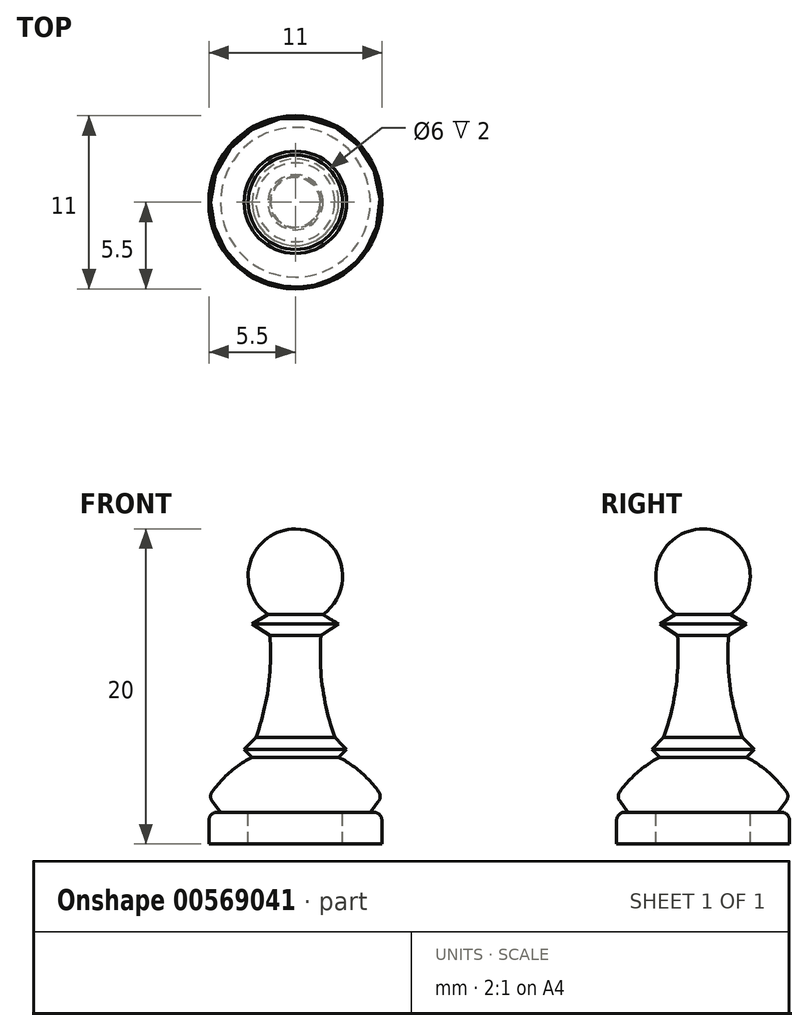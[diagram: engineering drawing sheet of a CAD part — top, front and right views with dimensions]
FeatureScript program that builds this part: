
annotation { "Feature Type Name" : "Feature", "Feature Type Description" : "" }
export const myFeature = defineFeature(function(context is Context, id is Id, definition is map)
    precondition{}
    {
        {
            var Q0;
            Q0=qCreatedBy(makeId("Front.planeOp"),FACE);
            var sketch = newSketch(context, id + "F0", { "sketchPlane" : qUnion([Q0])});
            skLineSegment(sketch, "E0", {"start": v(0, 0) * mm, "end": v(0, 20) * mm, "construction": true});
            skLineSegment(sketch, "E1", {"start": v(0, 20) * mm, "end": v(-2.87, 20) * mm, "construction": true});
            skArc(sketch, "E2", {"start": v(1.75, 14.56) * mm, "mid": v(2.86, 17.92) * mm, "end": v(0, 20) * mm});
            skLineSegment(sketch, "E3", {"start": v(1.75, 14.56) * mm, "end": v(2.75, 13.96) * mm});
            skLineSegment(sketch, "E4", {"start": v(2.75, 13.96) * mm, "end": v(1.63, 13.25) * mm});
            skArc(sketch, "E5", {"start": v(1.63, 13.25) * mm, "mid": v(1.72, 9.95) * mm, "end": v(2.5, 6.75) * mm});
            skLineSegment(sketch, "E6", {"start": v(2.5, 6.75) * mm, "end": v(3.25, 6) * mm});
            skLineSegment(sketch, "E7", {"start": v(3.25, 6) * mm, "end": v(2.75, 5.5) * mm});
            skArc(sketch, "E8", {"start": v(5.5, 3) * mm, "mid": v(4.29, 4.43) * mm, "end": v(2.75, 5.5) * mm});
            skLineSegment(sketch, "E9", {"start": v(5.5, 3) * mm, "end": v(4.76, 2) * mm});
            skLineSegment(sketch, "E10", {"start": v(4.76, 2) * mm, "end": v(5.48, 2) * mm});
            skLineSegment(sketch, "E11", {"start": v(5.48, 2) * mm, "end": v(5.5, 0) * mm});
            skLineSegment(sketch, "E12", {"start": v(5.5, 0) * mm, "end": v(3, 0) * mm});
            skLineSegment(sketch, "E13", {"start": v(0, 20) * mm, "end": v(0, 2) * mm});
            skLineSegment(sketch, "E14", {"start": v(0, 28.83) * mm, "end": v(0, -16.82) * mm, "construction": true});
            skLineSegment(sketch, "E15", {"start": v(3, 0) * mm, "end": v(3, 2) * mm});
            skLineSegment(sketch, "E16", {"start": v(3, 2) * mm, "end": v(0, 2) * mm});
            skSolve(sketch);
        }
        {
            var Q0;
            Q0=qSketchRegion(id+"F0",true);
            var Q1;
            Q1=sQuery(id+"F0.wireOp",EDGE,"E14");
            revolve(context, id + "F1", {"entities" : qUnion([Q0]), "axis" : qUnion([Q1]), "revolveType" : RevolveType.FULL});
        }
        {
            var Q0;
            Q0=makeQuery(id+"F1.opRevolve","SWEPT_EDGE",EDGE,{"disambiguationData":[OSD([sQuery(id+"F0.wireOp",EDGE,"E8"),sQuery(id+"F0.wireOp",EDGE,"E9")])]});
            var Q1;
            Q1=makeQuery(id+"F1.opRevolve","SWEPT_EDGE",EDGE,{"disambiguationData":[OSD([sQuery(id+"F0.wireOp",EDGE,"E10"),sQuery(id+"F0.wireOp",EDGE,"E11")])]});
            fillet(context, id + "F2", {"entities" : qUnion([Q0, Q1]), "radius" : .5 * mm, "tangentPropagation" : true, "allowEdgeOverflow" : false});
        }
    });
